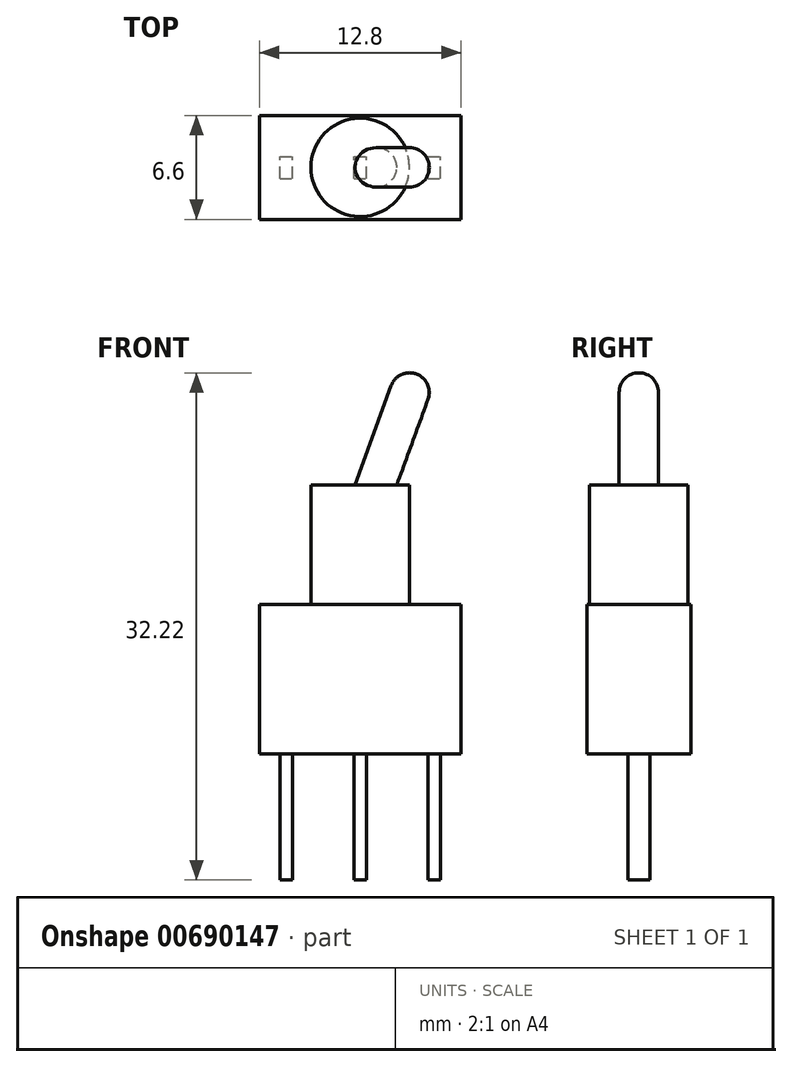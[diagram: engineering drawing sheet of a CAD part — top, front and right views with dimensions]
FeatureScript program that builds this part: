
annotation { "Feature Type Name" : "Feature", "Feature Type Description" : "" }
export const myFeature = defineFeature(function(context is Context, id is Id, definition is map)
    precondition{}
    {
        {
            var Q0;
            Q0=qCreatedBy(makeId("Front.planeOp"),FACE);
            var sketch = newSketch(context, id + "F0", { "sketchPlane" : qUnion([Q0])});
            skLineSegment(sketch, "E0.bottom", {"start": v(-6.4, 0) * mm, "end": v(6.4, 0) * mm});
            skLineSegment(sketch, "E0.top", {"start": v(-6.4, -9.5) * mm, "end": v(6.4, -9.5) * mm});
            skLineSegment(sketch, "E0.left", {"start": v(-6.4, 0) * mm, "end": v(-6.4, -9.5) * mm});
            skLineSegment(sketch, "E0.right", {"start": v(6.4, 0) * mm, "end": v(6.4, -9.5) * mm});
            skLineSegment(sketch, "E1", {"start": v(-0.4, -9.5) * mm, "end": v(-0.4, -17.5) * mm});
            skLineSegment(sketch, "E2", {"start": v(-0.4, -17.5) * mm, "end": v(0.4, -17.5) * mm});
            skLineSegment(sketch, "E3", {"start": v(0.4, -17.5) * mm, "end": v(0.4, -9.5) * mm});
            skLineSegment(sketch, "E4", {"start": v(4.3, -9.5) * mm, "end": v(4.3, -17.5) * mm});
            skLineSegment(sketch, "E5", {"start": v(4.3, -17.5) * mm, "end": v(5.1, -17.5) * mm});
            skLineSegment(sketch, "E6", {"start": v(5.1, -17.5) * mm, "end": v(5.1, -9.5) * mm});
            skLineSegment(sketch, "E7", {"start": v(-3.12, 0) * mm, "end": v(-3.13, 7.6) * mm});
            skLineSegment(sketch, "E8", {"start": v(-3.13, 7.6) * mm, "end": v(3.13, 7.6) * mm});
            skLineSegment(sketch, "E9", {"start": v(3.12, 7.6) * mm, "end": v(3.13, 0) * mm});
            skLineSegment(sketch, "E10", {"start": v(0, 0) * mm, "end": v(0, 7.6) * mm});
            skLineSegment(sketch, "E11.MirrorCS", {"start": v(-4.3, -9.5) * mm, "end": v(-4.3, -17.5) * mm});
            skLineSegment(sketch, "E12.MirrorCS", {"start": v(-4.3, -17.5) * mm, "end": v(-5.1, -17.5) * mm});
            skLineSegment(sketch, "E13.MirrorCS", {"start": v(-5.1, -17.5) * mm, "end": v(-5.1, -9.5) * mm});
            skLineSegment(sketch, "E14", {"start": v(2.33, 7.6) * mm, "end": v(4.31, 13.05) * mm});
            skLineSegment(sketch, "E15", {"start": v(1.96, 13.9) * mm, "end": v(-0.33, 7.6) * mm});
            skArc(sketch, "E16", {"start": v(4.31, 13.05) * mm, "mid": v(3.57, 14.65) * mm, "end": v(1.96, 13.9) * mm});
            skLineSegment(sketch, "E17", {"start": v(3.57, 14.65) * mm, "end": v(1, 7.6) * mm});
            skSolve(sketch);
        }
        {
            var Q0;
            {var subQ5=sQuery(id+"F0.wireOp",EDGE,"E0.left");Q0=makeQuery(id+"F0.imprint","IMPRINT",FACE,{"disambiguationData":[TD([[makeQuery(id+"F0.imprint","IMPRINT",EDGE,{"derivedFrom":subQ5}),1.0]])]});}
            extrude(context, id + "F1", {"entities" : qUnion([Q0]), "endBound" : BoundingType.SYMMETRIC, "depth" : 6.6 * mm, "offsetDistance" : 25 * mm});
        }
        {
            var Q0;
            {var subQ0=sQuery(id+"F0.wireOp",EDGE,"E11.MirrorCS");Q0=makeQuery(id+"F0.imprint","IMPRINT",FACE,{"disambiguationData":[TD([[makeQuery(id+"F0.imprint","IMPRINT",EDGE,{"derivedFrom":subQ0}),-1.0]])]});}
            var Q1;
            {var subQ2=sQuery(id+"F0.wireOp",EDGE,"E1");Q1=makeQuery(id+"F0.imprint","IMPRINT",FACE,{"disambiguationData":[TD([[makeQuery(id+"F0.imprint","IMPRINT",EDGE,{"derivedFrom":subQ2}),1.0]])]});}
            var Q2;
            {var subQ0=sQuery(id+"F0.wireOp",EDGE,"E4");Q2=makeQuery(id+"F0.imprint","IMPRINT",FACE,{"disambiguationData":[TD([[makeQuery(id+"F0.imprint","IMPRINT",EDGE,{"derivedFrom":subQ0}),1.0]])]});}
            extrude(context, id + "F2", {"entities" : qUnion([Q0, Q1, Q2]), "operationType" : NewBodyOperationType.ADD, "endBound" : BoundingType.SYMMETRIC, "depth" : 1.4 * mm, "offsetDistance" : 25 * mm});
        }
        {
            var Q0;
            {var subQ1=sQuery(id+"F0.wireOp",EDGE,"E7");Q0=makeQuery(id+"F0.imprint","IMPRINT",FACE,{"disambiguationData":[TD([[makeQuery(id+"F0.imprint","IMPRINT",EDGE,{"derivedFrom":subQ1}),-1.0]])]});}
            var Q1;
            Q1=sQuery(id+"F0.wireOp",EDGE,"E10");
            revolve(context, id + "F3", {"operationType" : NewBodyOperationType.ADD, "surfaceOperationType" : NewSurfaceOperationType.NEW, "entities" : qUnion([Q0]), "axis" : qUnion([Q1]), "revolveType" : RevolveType.FULL});
        }
        {
            var Q0;
            {var subQ1=sQuery(id+"F0.wireOp",EDGE,"E15");Q0=makeQuery(id+"F0.imprint","IMPRINT",FACE,{"disambiguationData":[TD([[makeQuery(id+"F0.imprint","IMPRINT",EDGE,{"derivedFrom":subQ1}),1.0]])]});}
            var Q1;
            Q1=sQuery(id+"F0.wireOp",EDGE,"E17");
            revolve(context, id + "F4", {"operationType" : NewBodyOperationType.ADD, "surfaceOperationType" : NewSurfaceOperationType.NEW, "entities" : qUnion([Q0]), "axis" : qUnion([Q1]), "revolveType" : RevolveType.FULL});
        }
    });
